# Revit family: Squire SIT Series
name_source: partatom
category: Mechanical Equipment
revit_build: Autodesk Revit MEP 2013 (Build: 20120221_2030(x64)
units: mm (PartAtom-declared; Revit-internal decimal feet)

## types (6) — shared parameters
# of Electrical Connections = 0
Boiler In/Out Connection = 1"
Description = Squire Stainless Steel Indirect Water Heater
Manufacturer = Lochinvar
SES BIM Studio # = 201264901-13
Total Amps = 0
Total Amps-Heater and Pumps = 0
URL = http://www.lochinvar.com
Vertical Clearance = 12"
Voltage/Control = 0
Voltage/Heater = 0

## per-type parameters (varying)
| type | A_TANK HEIGHT | B_TANK DIAMETER | Clearance Height | D_Pressure Relief Valve Height | GALLON CAPACITY | G_Boiler Inlet Dist From Floor | H_Boiler Outlet Dist from Floor | Hot Water Outlet Height | Hot&Cold Water Pipe Radius | Hot/Cold Water Connection | INPUT RATE (BTUH) | I_Cold Water Inlet Dist From Floor | Pipe Dist From Center | Pressure Relief Valve Radial Location | RECOVERY (GPH) | Sensor Well Height | Sensor Well Radial Location | Tank Radius |
| SIT030 | 39 1/2" | 20" | 51 1/2" | 32 1/4" | 27 | 21 3/4" | 8 1/4" | 40" | 1/2" | 1" | 99,000 | 3" | 8" | -10 1/2" | 160 | 21 3/4" | -14" | 10" |
| SIT050 | 47" | 24" | 59" | 39 3/4" | 52 | 24 1/2" | 9 1/4" | 47 1/2" | 1/2" | 1" | 133,000 | 3 3/4" | 10" | -12 1/2" | 209 | 24 1/2" | -16" | 12" |
| SIT040 | 55 1/2" | 20" | 67 1/2" | 58 1/2" | 40 | 25 1/4" | 8 1/4" | 56" | 1/2" | 1" | 115,000 | 3" | 8" | -10 1/2" | 181 | 25 1/4" | -14" | 10" |
| SIT065 | 60" | 24" | 72" | 52 1/4" | 67 | 28" | 9 1/4" | 60 1/2" | 3/4" | 1 1/2" | 154,000 | 3 1/4" | 10" | -12 1/2" | 263 | 28" | -16" | 12" |
| SIT080 | 69 1/2" | 24" | 81 1/2" | 61 3/4" | 82 | 28" | 9 1/4" | 70" | 3/4" | 1 1/2" | 160,000 | 3 1/4" | 10" | -12 1/2" | 266 | 28" | -16" | 12" |
| SIT119 | 68 1/4" | 28" | 80 1/4" | 60 1/4" | 114 | 31 3/4" | 9 1/4" | 68 3/4" | 3/4" | 1 1/2" | 200,000 | 3 1/4" | 12" | -14 1/2" | 349 | 31 3/4" | -18" | 14" |

note: column(s) folded — value = type name in every type: MODEL NO., Model

## geometry (parser evidence)
native form markers: Sweep x1
no freeform markers — native parametric forms only
